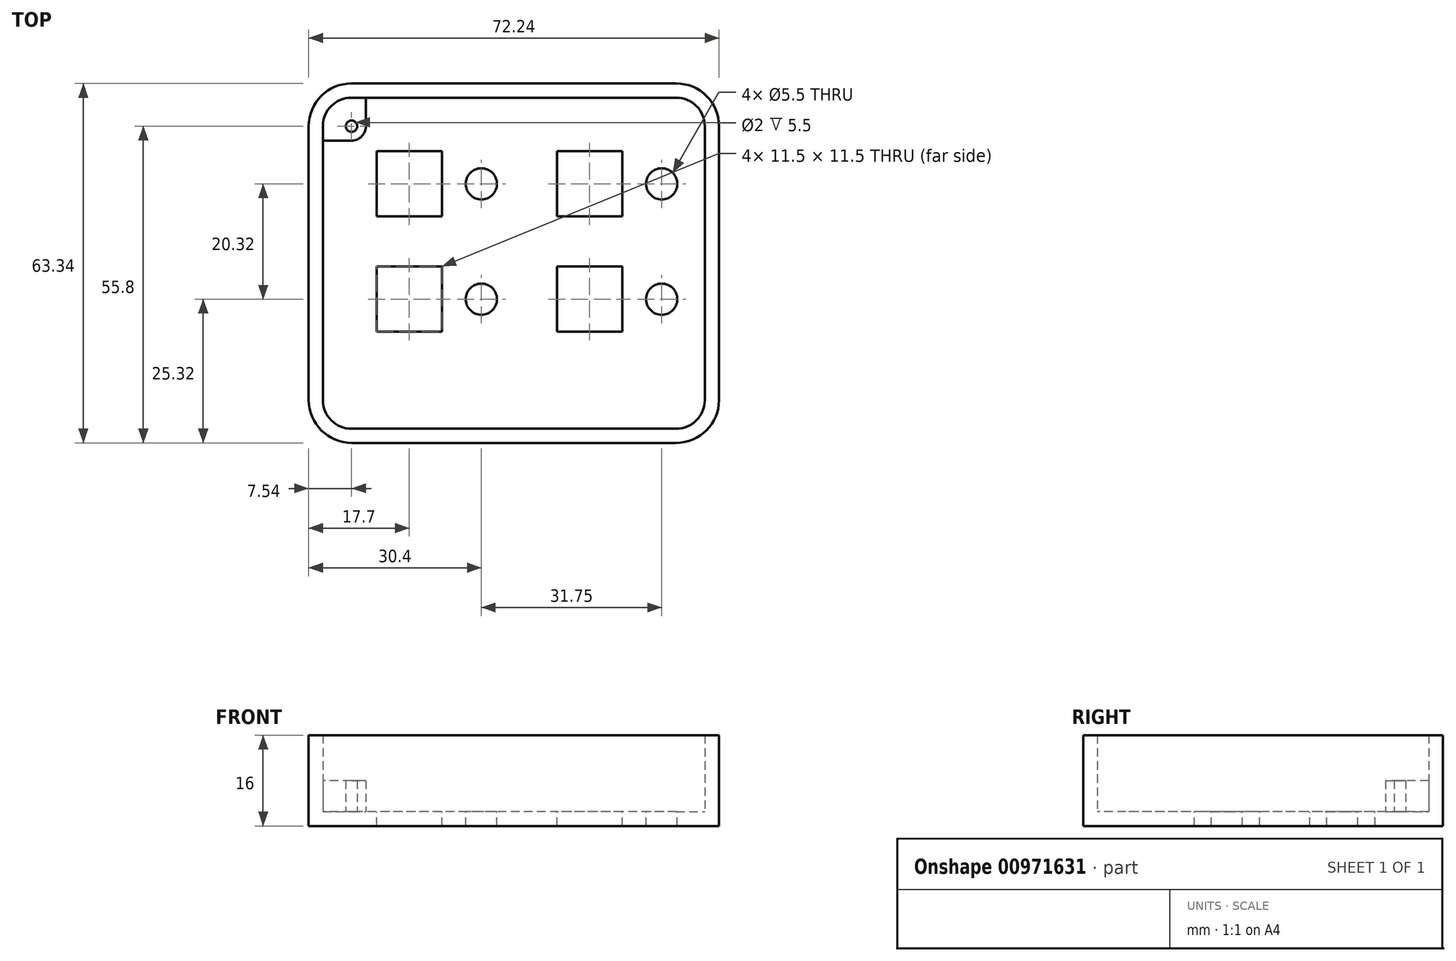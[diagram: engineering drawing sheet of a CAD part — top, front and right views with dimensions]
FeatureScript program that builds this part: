
annotation { "Feature Type Name" : "Feature", "Feature Type Description" : "" }
export const myFeature = defineFeature(function(context is Context, id is Id, definition is map)
    precondition{}
    {
        {
            var Q0;
            Q0=qCreatedBy(makeId("Top.planeOp"),FACE);
            var sketch = newSketch(context, id + "F0", { "sketchPlane" : qUnion([Q0])});
            skLineSegment(sketch, "E0.bottom", {"start": v(28.58, 31.67) * mm, "end": v(-28.58, 31.67) * mm});
            skLineSegment(sketch, "E0.top", {"start": v(28.58, -31.67) * mm, "end": v(-28.58, -31.67) * mm});
            skLineSegment(sketch, "E0.left", {"start": v(36.12, 24.13) * mm, "end": v(36.12, -24.13) * mm});
            skLineSegment(sketch, "E0.right", {"start": v(-36.12, 24.13) * mm, "end": v(-36.12, -24.13) * mm});
            skPoint(sketch, "E0.middle", {"position": v(0, 0) * mm});
            skPoint(sketch, "E1.visualSharp", {"position": v(-36.12, 31.67) * mm});
            skArc(sketch, "E1.filletArc", {"start": v(-28.58, 31.67) * mm, "mid": v(-33.91, 29.46) * mm, "end": v(-36.12, 24.13) * mm});
            skPoint(sketch, "E2.visualSharp", {"position": v(36.12, 31.67) * mm});
            skArc(sketch, "E2.filletArc", {"start": v(36.12, 24.13) * mm, "mid": v(33.91, 29.46) * mm, "end": v(28.58, 31.67) * mm});
            skPoint(sketch, "E3.visualSharp", {"position": v(36.12, -31.67) * mm});
            skArc(sketch, "E3.filletArc", {"start": v(28.58, -31.67) * mm, "mid": v(33.91, -29.46) * mm, "end": v(36.12, -24.13) * mm});
            skPoint(sketch, "E4.visualSharp", {"position": v(-36.12, -31.67) * mm});
            skArc(sketch, "E4.filletArc", {"start": v(-36.12, -24.13) * mm, "mid": v(-33.91, -29.46) * mm, "end": v(-28.58, -31.67) * mm});
            skSolve(sketch);
        }
        {
            var Q0;
            Q0=makeQuery(id+"F0.imprint","IMPRINT",FACE,{"disambiguationData":[TD([[makeQuery(id+"F0.imprint","IMPRINT",EDGE,{"derivedFrom":sQuery(id+"F0.wireOp",EDGE,"E0.bottom")}),1.0]])]});
            extrude(context, id + "F1", {"entities" : qUnion([Q0]), "depth" : 16 * mm, "offsetDistance" : 25 * mm});
        }
        {
            var Q0;
            Q0=makeQuery(id+"F1.opExtrude","CAP_FACE",FACE,{"disambiguationData":[OSD([sQuery(id+"F0.wireOp",EDGE,"E0.bottom"),sQuery(id+"F0.wireOp",EDGE,"E0.top"),sQuery(id+"F0.wireOp",EDGE,"E0.left"),sQuery(id+"F0.wireOp",EDGE,"E0.right"),sQuery(id+"F0.wireOp",EDGE,"E1.filletArc"),sQuery(id+"F0.wireOp",EDGE,"E2.filletArc"),sQuery(id+"F0.wireOp",EDGE,"E3.filletArc"),sQuery(id+"F0.wireOp",EDGE,"E4.filletArc")])],"isStart":false});
            shell(context, id + "F2", {"entities" : qUnion([Q0]), "thickness" : 2.5 * mm});
        }
        {
            var Q0;
            Q0=makeQuery(id+"F2.opShell","OFFSET_FACE",FACE,{"disambiguationData":[OSD([sQuery(id+"F0.wireOp",EDGE,"E0.bottom"),sQuery(id+"F0.wireOp",EDGE,"E0.top"),sQuery(id+"F0.wireOp",EDGE,"E0.left"),sQuery(id+"F0.wireOp",EDGE,"E0.right"),sQuery(id+"F0.wireOp",EDGE,"E1.filletArc"),sQuery(id+"F0.wireOp",EDGE,"E2.filletArc"),sQuery(id+"F0.wireOp",EDGE,"E3.filletArc"),sQuery(id+"F0.wireOp",EDGE,"E4.filletArc")])]});
            var sketch = newSketch(context, id + "F3", { "sketchPlane" : qUnion([Q0])});
            skLineSegment(sketch, "E5", {"start": v(-26.04, 29.17) * mm, "end": v(-26.04, 24.13) * mm});
            skLineSegment(sketch, "E6", {"start": v(-28.58, 21.6) * mm, "end": v(-33.62, 21.6) * mm});
            skPoint(sketch, "E7.visualSharp", {"position": v(-26.04, 21.6) * mm});
            skArc(sketch, "E7.filletArc", {"start": v(-28.58, 21.6) * mm, "mid": v(-26.78, 22.33) * mm, "end": v(-26.04, 24.13) * mm});
            skCircle(sketch, "E8", {"center": v(-28.58, 24.13) * mm, "radius": 1 * mm});
            skSolve(sketch);
        }
        {
            var Q0;
            {var subQ5=sQuery(id+"F3.wireOp",EDGE,"E5");Q0=makeQuery(id+"F3.imprint","IMPRINT",FACE,{"disambiguationData":[TD([[makeQuery(id+"F3.imprint","IMPRINT",EDGE,{"derivedFrom":subQ5}),-1.0]])]});}
            extrude(context, id + "F4", {"entities" : qUnion([Q0]), "operationType" : NewBodyOperationType.ADD, "depth" : 5.5 * mm, "offsetDistance" : 25 * mm});
        }
        {
            var Q0;
            {var subQ6=sQuery(id+"F0.wireOp",EDGE,"E0.top");var subQ9=sQuery(id+"F0.wireOp",EDGE,"E0.right");var subQ11=sQuery(id+"F0.wireOp",EDGE,"E0.bottom");var subQ12=makeQuery(id+"F2.opShell","OFFSET_FACE",FACE,{"disambiguationData":[OSD([subQ11])]});var subQ14=sQuery(id+"F0.wireOp",EDGE,"E0.left");var subQ20=sQuery(id+"F0.wireOp",EDGE,"E3.filletArc");var subQ22=sQuery(id+"F0.wireOp",EDGE,"E4.filletArc");var subQ24=sQuery(id+"F0.wireOp",EDGE,"E2.filletArc");Q0=makeQuery(id+"FwIHBaso8G06VOa_1.1.Fn2eGp5NWDbMN13_1.1.F4.boolean.opBoolean","SPLIT",FACE,{"disambiguationData":[TD([subQ12])],"derivedFrom":makeQuery(id+"FwIHBaso8G06VOa_1.1.F4.boolean.opBoolean","SPLIT",FACE,{"disambiguationData":[TD([subQ12])],"derivedFrom":makeQuery(id+"Fn2eGp5NWDbMN13_1.1.F4.boolean.opBoolean","SPLIT",FACE,{"disambiguationData":[TD([subQ12])],"derivedFrom":makeQuery(id+"F4.boolean.opBoolean","SPLIT",FACE,{"disambiguationData":[TD([subQ12])],"derivedFrom":makeQuery(id+"F2.opShell","OFFSET_FACE",FACE,{"disambiguationData":[OSD([subQ11,subQ6,subQ14,subQ9,sQuery(id+"F0.wireOp",EDGE,"E1.filletArc"),subQ24,subQ20,subQ22])]})})})})});}
            var sketch = newSketch(context, id + "F5", { "sketchPlane" : qUnion([Q0])});
            skLineSegment(sketch, "E9.bottom", {"start": v(-12.67, 19.72) * mm, "end": v(-24.17, 19.72) * mm});
            skLineSegment(sketch, "E9.top", {"start": v(-12.67, 8.22) * mm, "end": v(-24.17, 8.22) * mm});
            skLineSegment(sketch, "E9.left", {"start": v(-12.67, 19.72) * mm, "end": v(-12.67, 8.22) * mm});
            skLineSegment(sketch, "E9.right", {"start": v(-24.17, 19.72) * mm, "end": v(-24.17, 8.22) * mm});
            skPoint(sketch, "E9.middle", {"position": v(-18.42, 13.97) * mm});
            skCircle(sketch, "E10", {"center": v(-5.72, 13.97) * mm, "radius": 2.75 * mm});
            skLineSegment(sketch, "E11.0.1.0", {"start": v(-12.67, -0.6) * mm, "end": v(-24.17, -0.6) * mm});
            skPoint(sketch, "E11.0.1.1", {"position": v(-18.42, -6.35) * mm});
            skLineSegment(sketch, "E11.0.1.2", {"start": v(-12.67, -0.6) * mm, "end": v(-12.67, -12.1) * mm});
            skLineSegment(sketch, "E11.0.1.3", {"start": v(-24.17, -0.6) * mm, "end": v(-24.17, -12.1) * mm});
            skLineSegment(sketch, "E11.0.1.4", {"start": v(-12.67, -12.1) * mm, "end": v(-24.17, -12.1) * mm});
            skCircle(sketch, "E11.0.1.5", {"center": v(-5.72, -6.35) * mm, "radius": 2.75 * mm});
            skLineSegment(sketch, "E11.1.0.0", {"start": v(19.08, 19.72) * mm, "end": v(7.58, 19.72) * mm});
            skPoint(sketch, "E11.1.0.1", {"position": v(13.33, 13.97) * mm});
            skLineSegment(sketch, "E11.1.0.2", {"start": v(19.08, 19.72) * mm, "end": v(19.08, 8.22) * mm});
            skLineSegment(sketch, "E11.1.0.3", {"start": v(7.58, 19.72) * mm, "end": v(7.58, 8.22) * mm});
            skLineSegment(sketch, "E11.1.0.4", {"start": v(19.08, 8.22) * mm, "end": v(7.58, 8.22) * mm});
            skCircle(sketch, "E11.1.0.5", {"center": v(26.03, 13.97) * mm, "radius": 2.75 * mm});
            skLineSegment(sketch, "E11.1.1.0", {"start": v(19.08, -0.6) * mm, "end": v(7.58, -0.6) * mm});
            skPoint(sketch, "E11.1.1.1", {"position": v(13.33, -6.35) * mm});
            skLineSegment(sketch, "E11.1.1.2", {"start": v(19.08, -0.6) * mm, "end": v(19.08, -12.1) * mm});
            skLineSegment(sketch, "E11.1.1.3", {"start": v(7.58, -0.6) * mm, "end": v(7.58, -12.1) * mm});
            skLineSegment(sketch, "E11.1.1.4", {"start": v(19.08, -12.1) * mm, "end": v(7.58, -12.1) * mm});
            skCircle(sketch, "E11.1.1.5", {"center": v(26.03, -6.35) * mm, "radius": 2.75 * mm});
            skLineSegment(sketch, "E11.direction1", {"start": v(-24.17, 8.22) * mm, "end": v(7.58, 8.22) * mm, "construction": true});
            skLineSegment(sketch, "E11.direction2", {"start": v(-24.17, 8.22) * mm, "end": v(-24.17, -12.1) * mm, "construction": true});
            skSolve(sketch);
        }
        {
            var Q0;
            Q0 = qSketchRegion(id + "F5", true);
            extrude(context, id + "F6", {"entities" : qUnion([Q0]), "operationType" : NewBodyOperationType.REMOVE, "endBound" : BoundingType.THROUGH_ALL, "oppositeDirection" : true, "depth" : 25 * mm, "offsetDistance" : 25 * mm});
        }
    });
